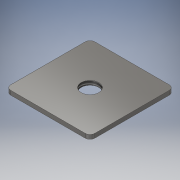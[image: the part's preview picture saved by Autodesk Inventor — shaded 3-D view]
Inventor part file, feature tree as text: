
AUTODESK INVENTOR PART (.ipt)
format: ipt  version: 2017 (Build 210142000, 142)  size: 111,616 bytes
history: native  units: mm
features: reference x8, other x3, sketch x2, sheet_metal_op x1, hole x1
ambient origin geometry x8: Origin, YZ Plane, XZ Plane, XY Plane, X Axis, Y Axis, Z Axis, Center Point
bodies: Solid1 (feature_tree)
feature tree (15):
  sheet_metal_op  "Face1"
  hole  "Hole1"  [1 undecoded]
  sketch  "Sketch1"  dims[d0=2.0mm]
  reference  "Reference1"
  reference  "Reference2"
  reference  "Reference3"
  reference  "Reference4"
  reference  "Reference5"
  reference  "Reference6"
  reference  "Reference7"
  reference  "Reference8"
  other  "Plate1"
  sketch  "Sketch3"  dims[d1=8.376mm d2=20.0mm d3=4.0mm d4=2.0mm d5=90.0deg d6=2.0mm d7=20.594885mm]
  other  "Bancada de Lavagem - 4240 x 780 x 900h.iam"
  other  "Tubular Quadrado - 40x40x1,5 - 820m:1"
note: 1 required parameter value undecoded (feature->parameter linkage not recoverable at this tier; creation-order binding heuristic only, values carry confidence <= 0.55)
